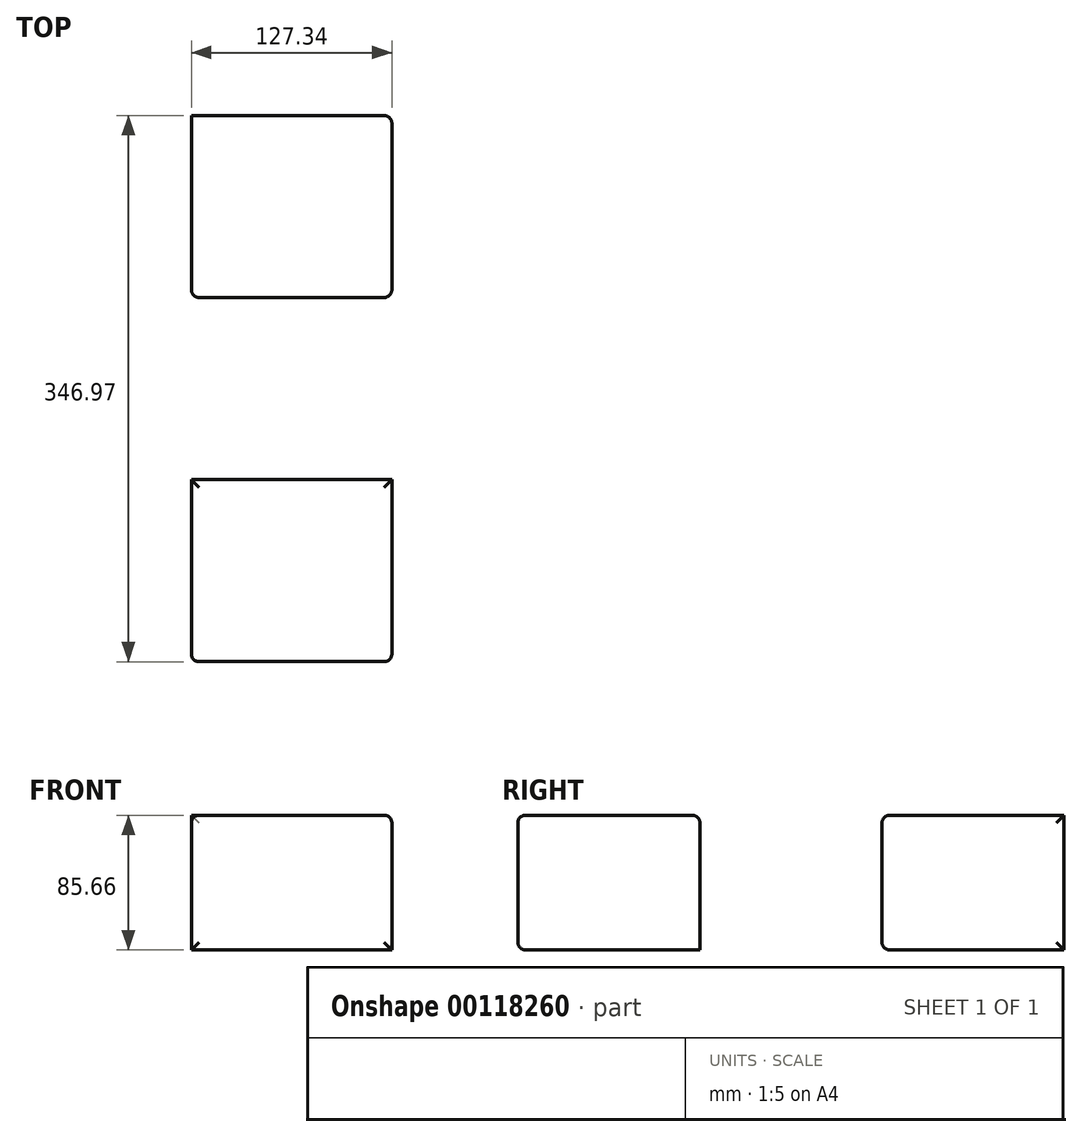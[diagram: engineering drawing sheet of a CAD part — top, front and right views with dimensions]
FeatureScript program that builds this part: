
annotation { "Feature Type Name" : "Feature", "Feature Type Description" : "" }
export const myFeature = defineFeature(function(context is Context, id is Id, definition is map)
    precondition{}
    {
        {
            var Q0;
            Q0=qCreatedBy(makeId("Top.planeOp"),FACE);
            var sketch = newSketch(context, id + "F0", { "sketchPlane" : qUnion([Q0])});
            skLineSegment(sketch, "E0.bottom", {"start": v(63.67, -57.83) * mm, "end": v(-63.67, -57.83) * mm});
            skLineSegment(sketch, "E0.top", {"start": v(63.67, 57.83) * mm, "end": v(-63.67, 57.83) * mm});
            skLineSegment(sketch, "E0.left", {"start": v(63.67, -57.83) * mm, "end": v(63.67, 57.83) * mm});
            skLineSegment(sketch, "E0.right", {"start": v(-63.67, -57.83) * mm, "end": v(-63.67, 57.83) * mm});
            skPoint(sketch, "E0.middle", {"position": v(0, 0) * mm});
            skSolve(sketch);
        }
        {
            var Q0;
            Q0 = qSketchRegion(id + "F0", true);
            extrude(context, id + "F1", {"entities" : qUnion([Q0]), "depth" : 85.66 * mm});
        }
        {
            var Q0;
            Q0=makeQuery(id+"F1.opExtrude","SWEPT_BODY",BODY,{"disambiguationData":[OSD([sQuery(id+"F0.wireOp",EDGE,"E0.bottom"),sQuery(id+"F0.wireOp",EDGE,"E0.top"),sQuery(id+"F0.wireOp",EDGE,"E0.left"),sQuery(id+"F0.wireOp",EDGE,"E0.right")])]});
            var Q1;
            Q1=makeQuery(id+"F1.opExtrude","CAP_EDGE",EDGE,{"disambiguationData":[OSD([sQuery(id+"F0.wireOp",EDGE,"E0.left")])],"isStart":true});
            transform(context, id + "F2", {"entities" : qUnion([Q0]), "transformType" : TransformType.TRANSLATION_ENTITY, "oppositeDirectionEntity" : false, "transformLine" : qUnion([Q1]), "makeCopy" : true});
        }
        {
            var Q0;
            Q0=makeQuery(id+"F2.opPattern","COPY",BODY,{"derivedFrom":makeQuery(id+"F1.opExtrude","SWEPT_BODY",BODY,{"disambiguationData":[OSD([sQuery(id+"F0.wireOp",EDGE,"E0.bottom"),sQuery(id+"F0.wireOp",EDGE,"E0.top"),sQuery(id+"F0.wireOp",EDGE,"E0.left"),sQuery(id+"F0.wireOp",EDGE,"E0.right")])]}),"instanceName":"1"});
            var Q1;
            Q1=makeQuery(id+"F1.opExtrude","CAP_EDGE",EDGE,{"disambiguationData":[OSD([sQuery(id+"F0.wireOp",EDGE,"E0.left")])],"isStart":true});
            transform(context, id + "F3", {"entities" : qUnion([Q0]), "transformType" : TransformType.TRANSLATION_ENTITY, "oppositeDirectionEntity" : false, "transformLine" : qUnion([Q1]), "makeCopy" : false});
        }
        {
            var Q0;
            Q0=makeQuery(id+"F2.opPattern","COPY",FACE,{"derivedFrom":makeQuery(id+"F1.opExtrude","SWEPT_FACE",FACE,{"disambiguationData":[OSD([sQuery(id+"F0.wireOp",EDGE,"E0.left")])]}),"instanceName":"1"});
            var Q1;
            Q1=makeQuery(id+"F2.opPattern","COPY",FACE,{"derivedFrom":makeQuery(id+"F1.opExtrude","SWEPT_FACE",FACE,{"disambiguationData":[OSD([sQuery(id+"F0.wireOp",EDGE,"E0.bottom")])]}),"instanceName":"1"});
            var Q2;
            Q2=makeQuery(id+"F1.opExtrude","CAP_EDGE",EDGE,{"disambiguationData":[OSD([sQuery(id+"F0.wireOp",EDGE,"E0.right")])],"isStart":false});
            var Q3;
            Q3=makeQuery(id+"F1.opExtrude","CAP_FACE",FACE,{"disambiguationData":[OSD([sQuery(id+"F0.wireOp",EDGE,"E0.bottom"),sQuery(id+"F0.wireOp",EDGE,"E0.top"),sQuery(id+"F0.wireOp",EDGE,"E0.left"),sQuery(id+"F0.wireOp",EDGE,"E0.right")])],"isStart":false});
            var Q4;
            Q4=makeQuery(id+"F1.opExtrude","SWEPT_FACE",FACE,{"disambiguationData":[OSD([sQuery(id+"F0.wireOp",EDGE,"E0.bottom")])]});
            fillet(context, id + "F4", {"entities" : qUnion([Q0, Q1, Q2, Q3, Q4]), "radius" : 5 * mm, "tangentPropagation" : true, "allowEdgeOverflow" : false});
        }
    });
